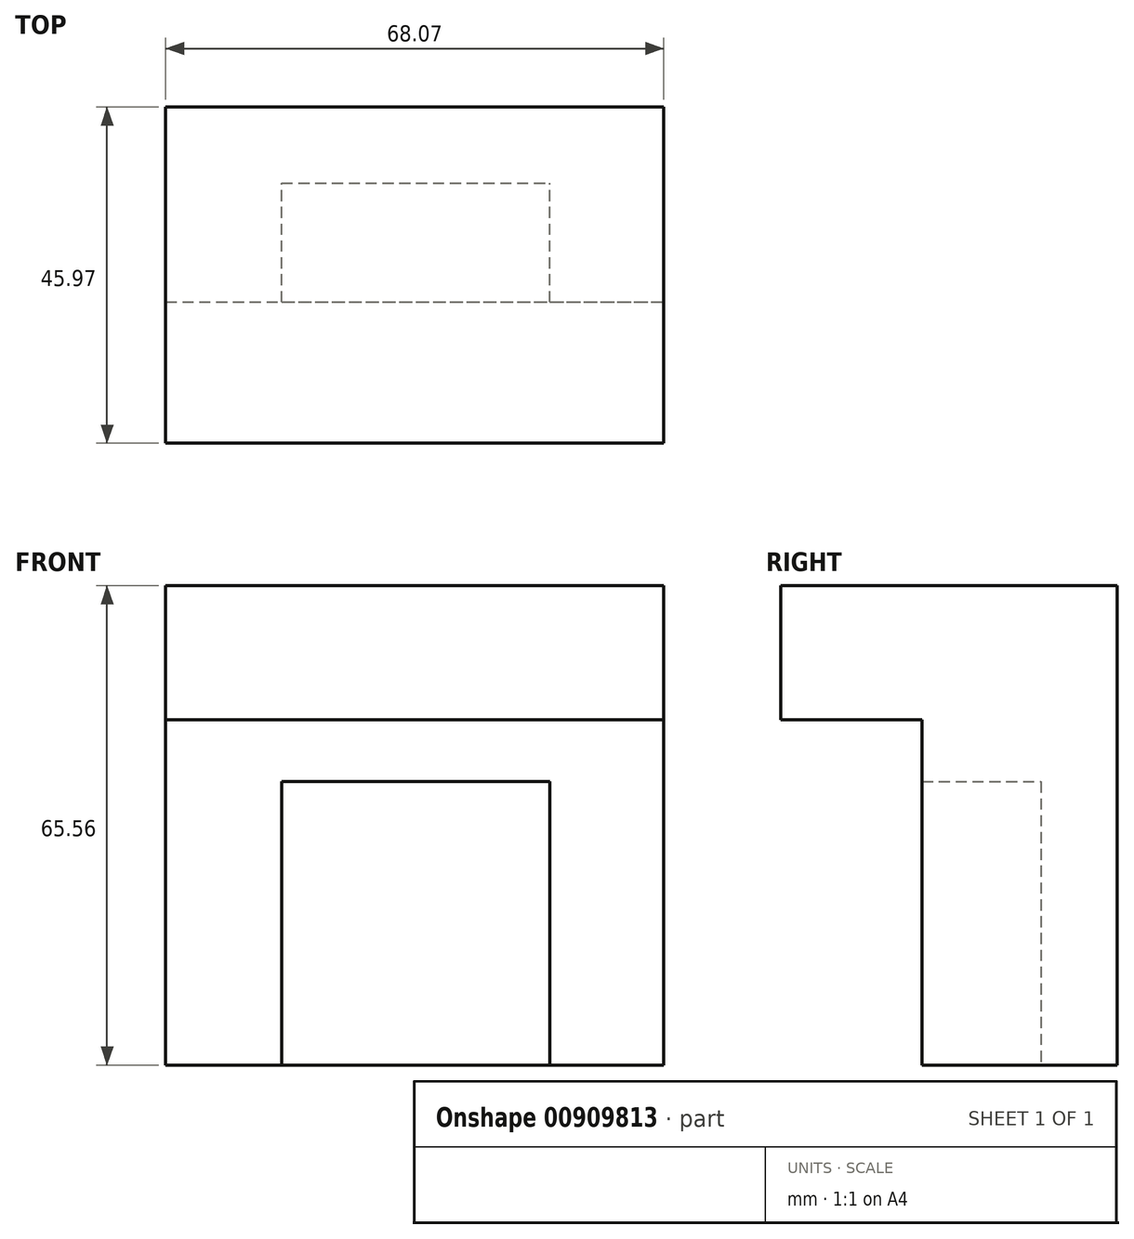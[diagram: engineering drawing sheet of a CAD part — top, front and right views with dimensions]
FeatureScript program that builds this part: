
annotation { "Feature Type Name" : "Feature", "Feature Type Description" : "" }
export const myFeature = defineFeature(function(context is Context, id is Id, definition is map)
    precondition{}
    {
        {
            var Q0;
            Q0=qCreatedBy(makeId("Front.planeOp"),FACE);
            var sketch = newSketch(context, id + "F0", { "sketchPlane" : qUnion([Q0])});
            skLineSegment(sketch, "E0.bottom", {"start": v(-30.98, 26.8) * mm, "end": v(37.09, 26.8) * mm});
            skLineSegment(sketch, "E0.top", {"start": v(-30.98, -38.75) * mm, "end": v(37.09, -38.75) * mm});
            skLineSegment(sketch, "E0.left", {"start": v(-30.98, 26.8) * mm, "end": v(-30.98, -38.75) * mm});
            skLineSegment(sketch, "E0.right", {"start": v(37.09, 26.8) * mm, "end": v(37.09, -38.75) * mm});
            skSolve(sketch);
        }
        {
            var Q0;
            Q0=makeQuery(id+"F0.imprint","IMPRINT",FACE,{"disambiguationData":[TD([[makeQuery(id+"F0.imprint","IMPRINT",EDGE,{"derivedFrom":sQuery(id+"F0.wireOp",EDGE,"E0.bottom")}),-1.0]])]});
            extrude(context, id + "F1", {"entities" : qUnion([Q0]), "depth" : 26.67 * mm, "offsetDistance" : 25.4 * mm});
        }
        {
            var Q0;
            Q0=makeQuery(id+"F1.opExtrude","CAP_FACE",FACE,{"disambiguationData":[OSD([sQuery(id+"F0.wireOp",EDGE,"E0.bottom"),sQuery(id+"F0.wireOp",EDGE,"E0.top"),sQuery(id+"F0.wireOp",EDGE,"E0.left"),sQuery(id+"F0.wireOp",EDGE,"E0.right")])],"isStart":false});
            var sketch = newSketch(context, id + "F2", { "sketchPlane" : qUnion([Q0])});
            skLineSegment(sketch, "E1.bottom", {"start": v(-15.14, 8.47) * mm, "end": v(21.53, 8.47) * mm});
            skLineSegment(sketch, "E1.top", {"start": v(-15.14, -38.75) * mm, "end": v(21.53, -38.75) * mm});
            skLineSegment(sketch, "E1.left", {"start": v(-15.14, 8.47) * mm, "end": v(-15.14, -38.75) * mm});
            skLineSegment(sketch, "E1.right", {"start": v(21.53, 8.47) * mm, "end": v(21.53, -38.75) * mm});
            skSolve(sketch);
        }
        {
            var Q0;
            Q0=makeQuery(id+"F2.imprint","IMPRINT",FACE,{"disambiguationData":[TD([[makeQuery(id+"F2.imprint","IMPRINT",EDGE,{"derivedFrom":sQuery(id+"F2.wireOp",EDGE,"E1.bottom")}),-1.0]])]});
            extrude(context, id + "F3", {"entities" : qUnion([Q0]), "operationType" : NewBodyOperationType.REMOVE, "oppositeDirection" : true, "depth" : 16.26 * mm, "offsetDistance" : 25.4 * mm});
        }
        {
            var Q0;
            Q0=makeQuery(id+"F1.opExtrude","CAP_FACE",FACE,{"disambiguationData":[OSD([sQuery(id+"F0.wireOp",EDGE,"E0.bottom"),sQuery(id+"F0.wireOp",EDGE,"E0.top"),sQuery(id+"F0.wireOp",EDGE,"E0.left"),sQuery(id+"F0.wireOp",EDGE,"E0.right")])],"isStart":false});
            var sketch = newSketch(context, id + "F4", { "sketchPlane" : qUnion([Q0])});
            skLineSegment(sketch, "E2.bottom", {"start": v(-30.98, 26.8) * mm, "end": v(37.09, 26.8) * mm});
            skLineSegment(sketch, "E2.top", {"start": v(-30.98, 8.47) * mm, "end": v(37.09, 8.47) * mm});
            skLineSegment(sketch, "E2.left", {"start": v(-30.98, 26.8) * mm, "end": v(-30.98, 8.47) * mm});
            skLineSegment(sketch, "E2.right", {"start": v(37.09, 26.8) * mm, "end": v(37.09, 8.47) * mm});
            skSolve(sketch);
        }
        {
            var Q0;
            Q0=makeQuery(id+"F4.imprint","IMPRINT",FACE,{"disambiguationData":[TD([[makeQuery(id+"F4.imprint","IMPRINT",EDGE,{"derivedFrom":sQuery(id+"F4.wireOp",EDGE,"E2.bottom")}),-1.0]])]});
            extrude(context, id + "F5", {"entities" : qUnion([Q0]), "operationType" : NewBodyOperationType.ADD, "depth" : 19.3 * mm, "offsetDistance" : 25.4 * mm});
        }
        {
            var Q0;
            Q0=makeQuery(id+"F3.boolean.opBoolean","COPY",FACE,{"derivedFrom":makeQuery(id+"F3.opExtrude","CAP_FACE",FACE,{"disambiguationData":[OSD([sQuery(id+"F2.wireOp",EDGE,"E1.bottom"),sQuery(id+"F2.wireOp",EDGE,"E1.top"),sQuery(id+"F2.wireOp",EDGE,"E1.left"),sQuery(id+"F2.wireOp",EDGE,"E1.right")])],"isStart":false})});
            var sketch = newSketch(context, id + "F6", { "sketchPlane" : qUnion([Q0])});
            skLineSegment(sketch, "E3.bottom", {"start": v(-15.14, 8.47) * mm, "end": v(21.53, 8.47) * mm});
            skLineSegment(sketch, "E3.top", {"start": v(-15.14, 0) * mm, "end": v(21.53, 0) * mm});
            skLineSegment(sketch, "E3.left", {"start": v(-15.14, 8.47) * mm, "end": v(-15.14, 0) * mm});
            skLineSegment(sketch, "E3.right", {"start": v(21.53, 8.47) * mm, "end": v(21.53, 0) * mm});
            skSolve(sketch);
        }
        {
            var Q0;
            Q0=makeQuery(id+"F6.imprint","IMPRINT",FACE,{"disambiguationData":[TD([[makeQuery(id+"F6.imprint","IMPRINT",EDGE,{"derivedFrom":sQuery(id+"F6.wireOp",EDGE,"E3.bottom")}),-1.0]])]});
            extrude(context, id + "F7", {"entities" : qUnion([Q0]), "operationType" : NewBodyOperationType.ADD, "depth" : 16.26 * mm, "offsetDistance" : 25.4 * mm});
        }
    });
